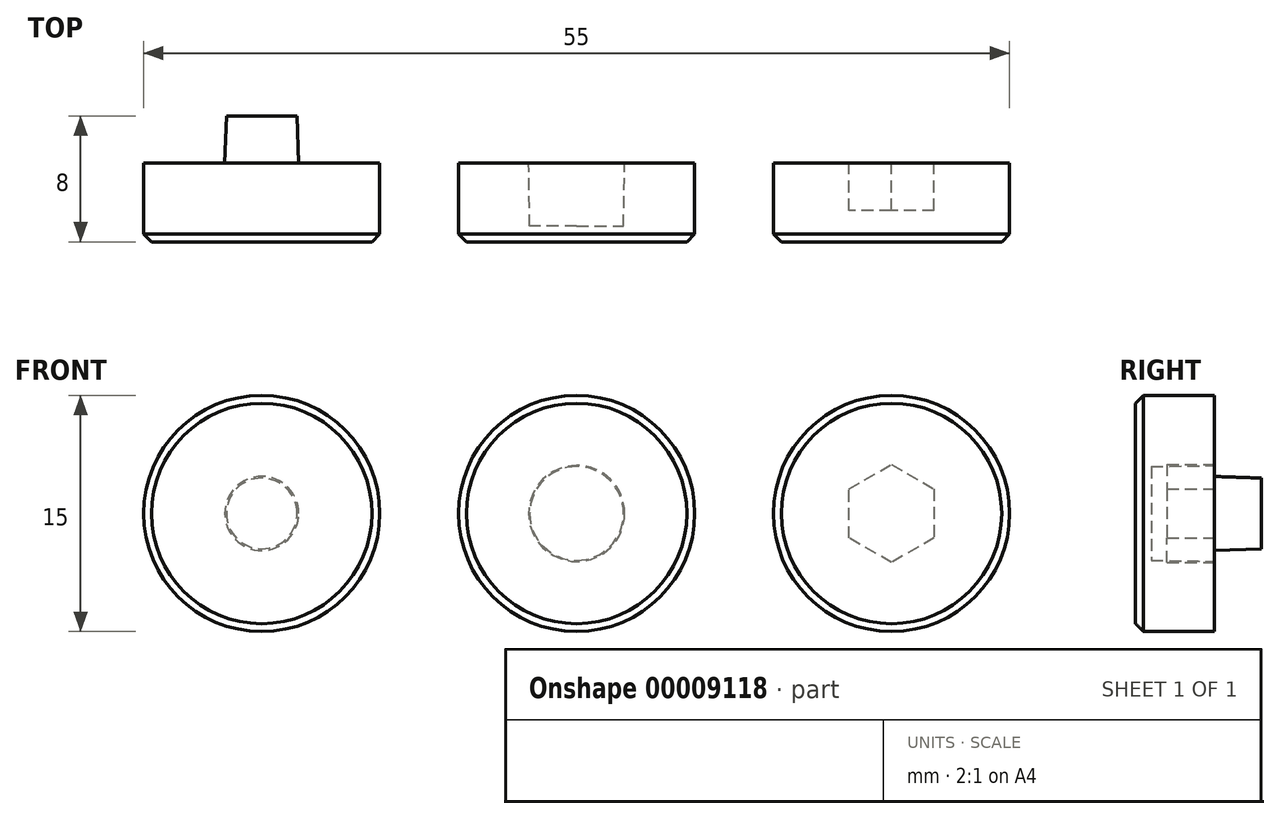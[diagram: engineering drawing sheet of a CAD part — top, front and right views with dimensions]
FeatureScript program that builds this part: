
annotation { "Feature Type Name" : "Feature", "Feature Type Description" : "" }
export const myFeature = defineFeature(function(context is Context, id is Id, definition is map)
    precondition{}
    {
        {
            var Q0;
            Q0=qCreatedBy(makeId("Front.planeOp"),FACE);
            var sketch = newSketch(context, id + "F0", { "sketchPlane" : qUnion([Q0])});
            skCircle(sketch, "E0", {"center": v(0, 0) * mm, "radius": 7.5 * mm});
            skSolve(sketch);
        }
        {
            var Q0;
            Q0=qSketchRegion(id+"F0",true);
            extrude(context, id + "F1", {"entities" : qUnion([Q0]), "depth" : 5 * mm});
        }
        {
            var Q0;
            Q0=makeQuery(id+"F1.opExtrude","CAP_FACE",FACE,{"disambiguationData":[OSD([sQuery(id+"F0.wireOp",EDGE,"E0")])],"isStart":true});
            var sketch = newSketch(context, id + "F2", { "sketchPlane" : qUnion([Q0])});
            skCircle(sketch, "E1", {"center": v(0, 0) * mm, "radius": 2.35 * mm});
            skSolve(sketch);
        }
        {
            var Q0;
            Q0=qSketchRegion(id+"F2",true);
            extrude(context, id + "F3", {"entities" : qUnion([Q0]), "operationType" : NewBodyOperationType.ADD, "depth" : 3 * mm, "hasDraft" : true, "draftAngle" : 2 * degree, "draftPullDirection" : true});
        }
        {
            var Q0;
            Q0=makeQuery(id+"F1.opExtrude","CAP_EDGE",EDGE,{"disambiguationData":[OSD([sQuery(id+"F0.wireOp",EDGE,"E0")])],"isStart":false});
            chamfer(context, id + "F4", {"entities" : qUnion([Q0]), "width" : 0.5 * mm, "tangentPropagation" : true});
        }
        {
            var Q0;
            Q0=makeQuery(id+"F1.opExtrude","SWEPT_BODY",BODY,{"disambiguationData":[OSD([sQuery(id+"F0.wireOp",EDGE,"E0")])]});
            transform(context, id + "F5", {"entities" : qUnion([Q0]), "transformType" : TransformType.TRANSLATION_3D, "dx" : 20 * mm, "dy" : 0 * mm, "dz" : 0 * mm, "makeCopy" : true});
        }
        {
            var Q0;
            Q0=makeQuery(id+"F5.opPattern","COPY",FACE,{"derivedFrom":makeQuery(id+"F3.opExtrude","CAP_FACE",FACE,{"disambiguationData":[OSD([sQuery(id+"F2.wireOp",EDGE,"E1")])],"isStart":false}),"instanceName":"1"});
            var sketch = newSketch(context, id + "F6", { "sketchPlane" : qUnion([Q0])});
            skCircle(sketch, "E2", {"center": v(-20, 0) * mm, "radius": 3.1 * mm});
            skSolve(sketch);
        }
        {
            var Q0;
            Q0 = qSketchRegion(id + "F6", true);
            extrude(context, id + "F7", {"entities" : qUnion([Q0]), "operationType" : NewBodyOperationType.REMOVE, "oppositeDirection" : true, "depth" : 7 * mm, "hasDraft" : true, "draftAngle" : 1 * degree, "draftPullDirection" : true});
        }
        {
            var Q0;
            Q0=makeQuery(id+"F1.opExtrude","SWEPT_BODY",BODY,{"disambiguationData":[OSD([sQuery(id+"F0.wireOp",EDGE,"E0")])]});
            transform(context, id + "F8", {"entities" : qUnion([Q0]), "transformType" : TransformType.TRANSLATION_3D, "dx" : 40 * mm, "dy" : 0 * mm, "dz" : 0 * mm, "makeCopy" : true});
        }
        {
            var Q0;
            Q0=makeQuery(id+"F8.opPattern","COPY",FACE,{"derivedFrom":makeQuery(id+"F3.opExtrude","CAP_FACE",FACE,{"disambiguationData":[OSD([sQuery(id+"F2.wireOp",EDGE,"E1")])],"isStart":false}),"instanceName":"1"});
            var sketch = newSketch(context, id + "F9", { "sketchPlane" : qUnion([Q0])});
            skCircle(sketch, "E3.cCircle", {"center": v(-40, 0) * mm, "radius": 2.7 * mm, "construction": true});
            skLineSegment(sketch, "E3.0", {"start": v(-37.3, 1.56) * mm, "end": v(-37.3, -1.56) * mm});
            skLineSegment(sketch, "E3.1", {"start": v(-37.3, -1.56) * mm, "end": v(-40, -3.12) * mm});
            skLineSegment(sketch, "E3.2", {"start": v(-40, -3.12) * mm, "end": v(-42.7, -1.56) * mm});
            skLineSegment(sketch, "E3.3", {"start": v(-42.7, -1.56) * mm, "end": v(-42.7, 1.56) * mm});
            skLineSegment(sketch, "E3.4", {"start": v(-42.7, 1.56) * mm, "end": v(-40, 3.12) * mm});
            skLineSegment(sketch, "E3.5", {"start": v(-40, 3.12) * mm, "end": v(-37.3, 1.56) * mm});
            skPoint(sketch, "E3.0.midPoint", {"position": v(-37.3, 0) * mm});
            skSolve(sketch);
        }
        {
            var Q0;
            Q0 = qSketchRegion(id + "F9", true);
            extrude(context, id + "F10", {"entities" : qUnion([Q0]), "operationType" : NewBodyOperationType.REMOVE, "oppositeDirection" : true, "depth" : 6 * mm});
        }
    });
